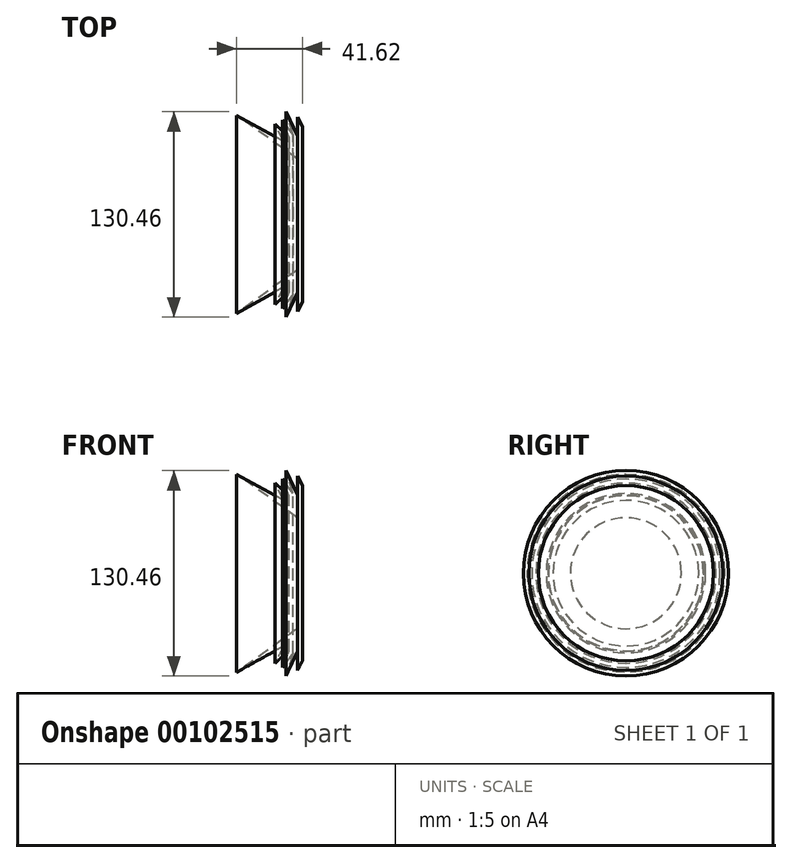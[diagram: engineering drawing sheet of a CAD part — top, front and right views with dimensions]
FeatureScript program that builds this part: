
annotation { "Feature Type Name" : "Feature", "Feature Type Description" : "" }
export const myFeature = defineFeature(function(context is Context, id is Id, definition is map)
    precondition{}
    {
        {
            var Q0;
            Q0=qCreatedBy(makeId("Front.planeOp"),FACE);
            var sketch = newSketch(context, id + "F0", { "sketchPlane" : qUnion([Q0])});
            skLineSegment(sketch, "E0", {"start": v(0, -35.25) * mm, "end": v(-3.13, -35.25) * mm});
            skLineSegment(sketch, "E1", {"start": v(-3.13, -35.25) * mm, "end": v(-3.13, 0) * mm});
            skLineSegment(sketch, "E2", {"start": v(-3.13, 0) * mm, "end": v(-41.62, 27.6) * mm});
            skLineSegment(sketch, "E3", {"start": v(-41.62, 27.6) * mm, "end": v(-11.85, 11) * mm});
            skLineSegment(sketch, "E4", {"start": v(-11.85, 11) * mm, "end": v(-17.4, 21.96) * mm});
            skLineSegment(sketch, "E5", {"start": v(-17.4, 21.96) * mm, "end": v(-8.55, 13.94) * mm});
            skLineSegment(sketch, "E6", {"start": v(-8.55, 13.94) * mm, "end": v(-12.48, 24.54) * mm});
            skLineSegment(sketch, "E7", {"start": v(-12.48, 24.54) * mm, "end": v(-5.87, 15.35) * mm});
            skLineSegment(sketch, "E8", {"start": v(-5.87, 15.35) * mm, "end": v(-10.33, 29.98) * mm});
            skLineSegment(sketch, "E9", {"start": v(-10.33, 29.98) * mm, "end": v(-3.06, 14.36) * mm});
            skLineSegment(sketch, "E10", {"start": v(-3.06, 14.36) * mm, "end": v(-3.06, 26.44) * mm});
            skLineSegment(sketch, "E11", {"start": v(-3.06, 26.44) * mm, "end": v(0, 20.4) * mm});
            skPoint(sketch, "E11.endSnap0", {"position": v(-3.06, 20.4) * mm});
            skLineSegment(sketch, "E12", {"start": v(0, 20.4) * mm, "end": v(0, -35.25) * mm});
            skSolve(sketch);
        }
        {
            var Q0;
            Q0=makeQuery(id+"F0.imprint","IMPRINT",FACE,{"disambiguationData":[TD([[makeQuery(id+"F0.imprint","IMPRINT",EDGE,{"derivedFrom":sQuery(id+"F0.wireOp",EDGE,"E0")}),-1.0]])]});
            var Q1;
            Q1=sQuery(id+"F0.wireOp",EDGE,"E0");
            revolve(context, id + "F1", {"entities" : qUnion([Q0]), "axis" : qUnion([Q1]), "revolveType" : RevolveType.FULL});
        }
    });
